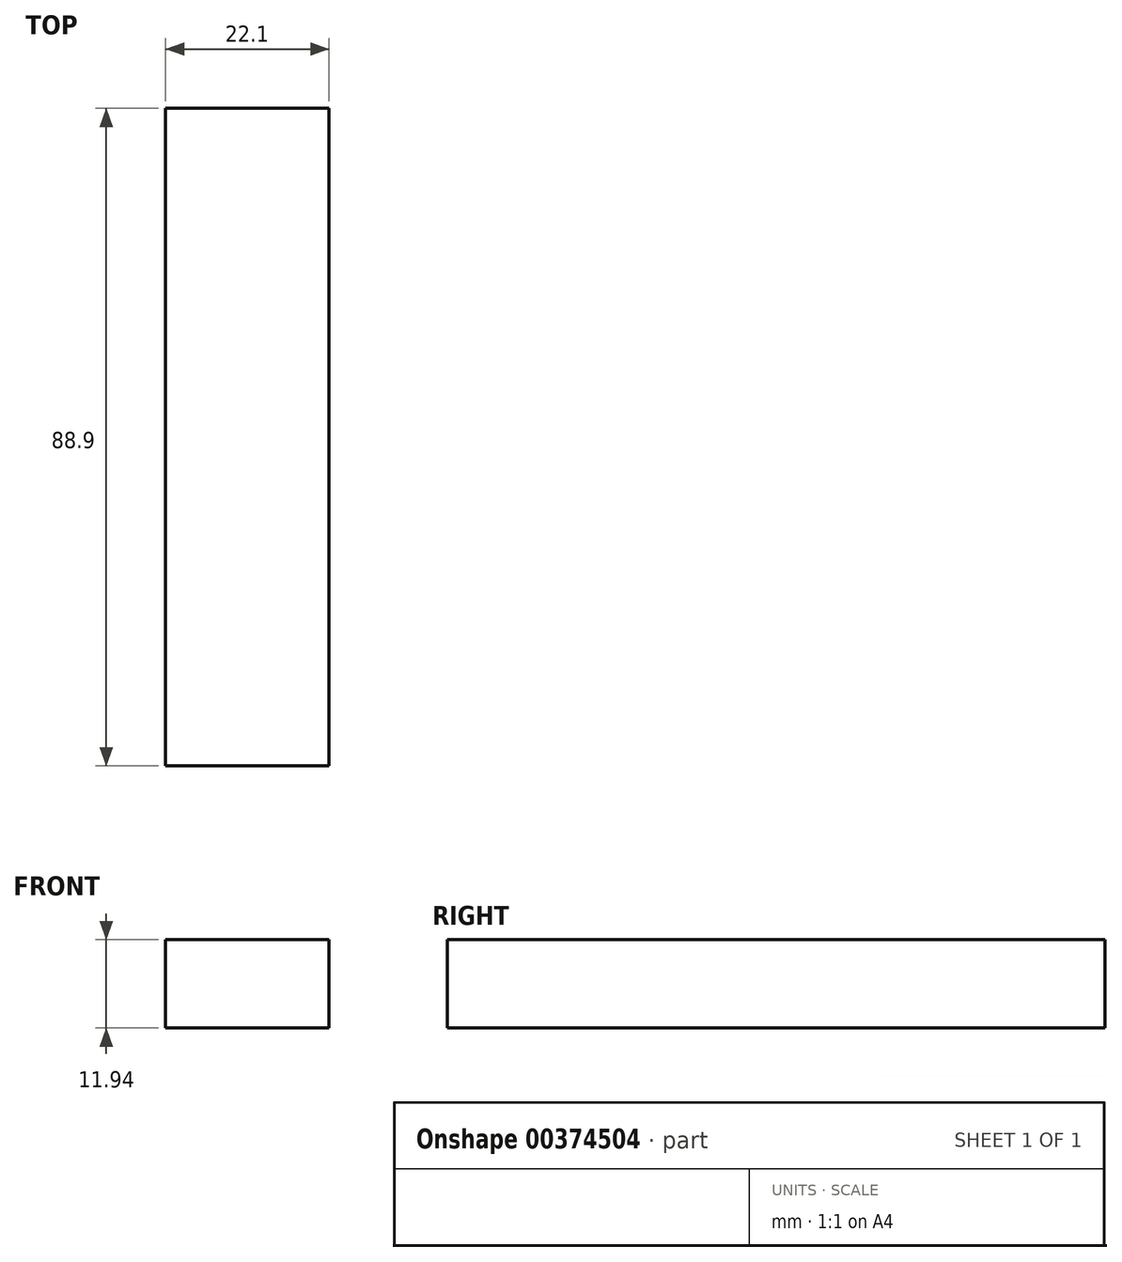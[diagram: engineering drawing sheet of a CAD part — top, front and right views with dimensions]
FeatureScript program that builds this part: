
annotation { "Feature Type Name" : "Feature", "Feature Type Description" : "" }
export const myFeature = defineFeature(function(context is Context, id is Id, definition is map)
    precondition{}
    {
        {
            var Q0;
            Q0=qCreatedBy(makeId("Top.planeOp"),FACE);
            var sketch = newSketch(context, id + "F0", { "sketchPlane" : qUnion([Q0])});
            skLineSegment(sketch, "E0.bottom", {"start": v(11.05, -44.45) * mm, "end": v(-11.05, -44.45) * mm});
            skLineSegment(sketch, "E0.top", {"start": v(11.05, 44.45) * mm, "end": v(-11.05, 44.45) * mm});
            skLineSegment(sketch, "E0.left", {"start": v(11.05, -44.45) * mm, "end": v(11.05, 44.45) * mm});
            skLineSegment(sketch, "E0.right", {"start": v(-11.05, -44.45) * mm, "end": v(-11.05, 44.45) * mm});
            skPoint(sketch, "E0.middle", {"position": v(0, 0) * mm});
            skSolve(sketch);
        }
        {
            var Q0;
            Q0 = qSketchRegion(id + "F0", true);
            extrude(context, id + "F1", {"entities" : qUnion([Q0]), "depth" : 11.94 * mm});
        }
    });
